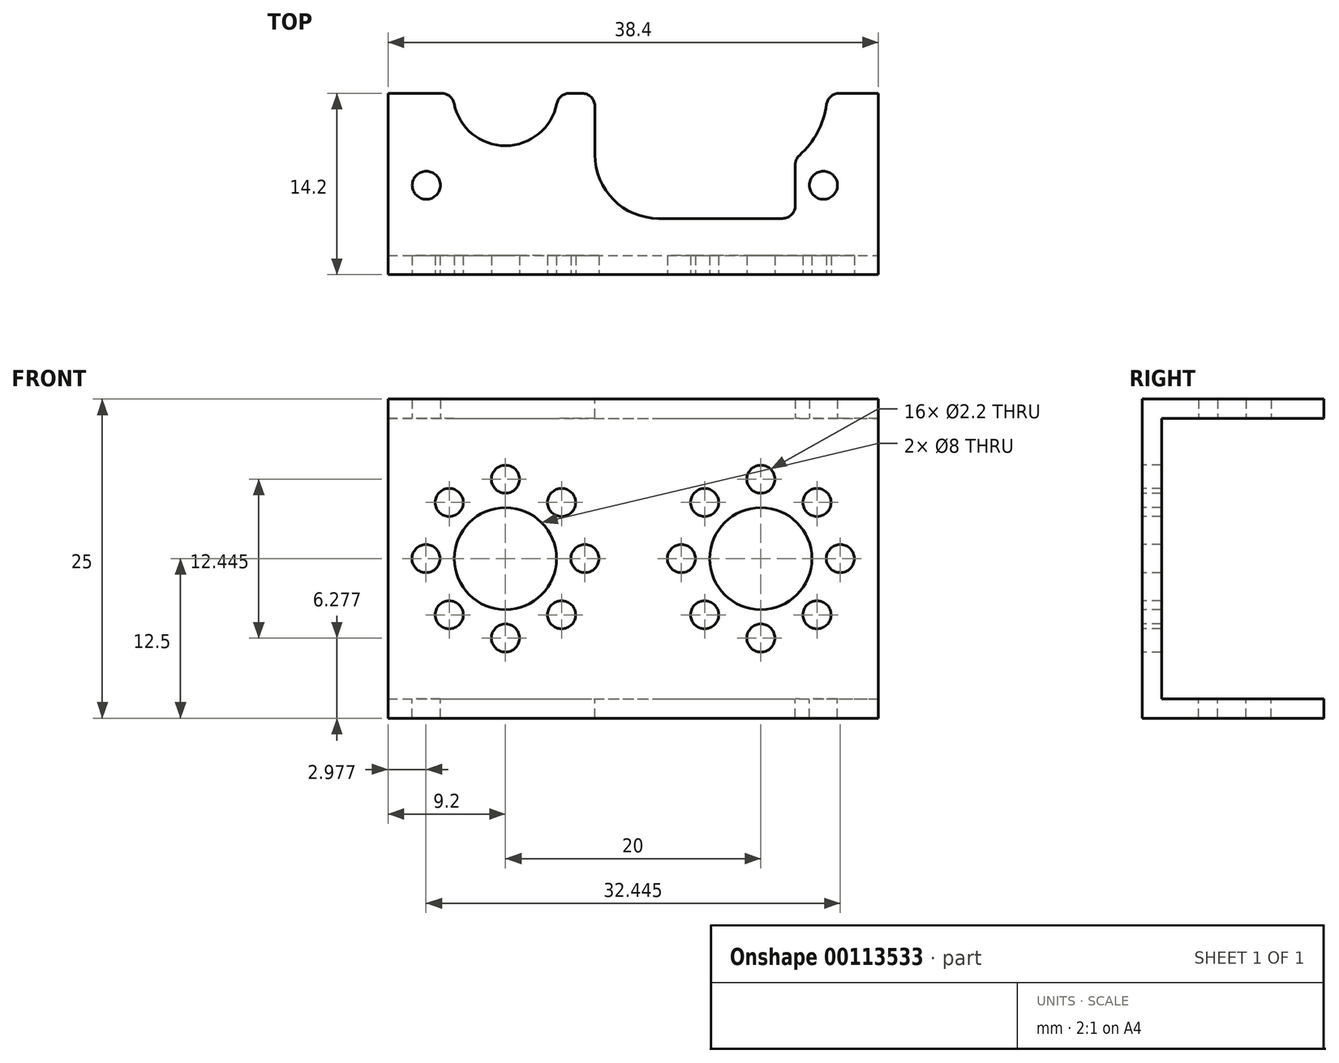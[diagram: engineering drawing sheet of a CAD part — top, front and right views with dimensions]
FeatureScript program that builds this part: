
annotation { "Feature Type Name" : "Feature", "Feature Type Description" : "" }
export const myFeature = defineFeature(function(context is Context, id is Id, definition is map)
    precondition{}
    {
        {
            var Q0;
            Q0=qCreatedBy(makeId("Top.planeOp"),FACE);
            var sketch = newSketch(context, id + "F0", { "sketchPlane" : qUnion([Q0])});
            skLineSegment(sketch, "E0.bottom", {"start": v(19.2, -14.2) * mm, "end": v(-19.2, -14.2) * mm});
            skLineSegment(sketch, "E0.top", {"start": v(19.2, 14.2) * mm, "end": v(-19.2, 14.2) * mm});
            skLineSegment(sketch, "E0.left", {"start": v(19.2, -14.2) * mm, "end": v(19.2, 14.2) * mm});
            skLineSegment(sketch, "E0.right", {"start": v(-19.2, -14.2) * mm, "end": v(-19.2, 14.2) * mm});
            skPoint(sketch, "E0.middle", {"position": v(0, 0) * mm});
            skCircle(sketch, "E1", {"center": v(-10, 0) * mm, "radius": 4.1 * mm});
            skCircle(sketch, "E2", {"center": v(-16.2, 7.2) * mm, "radius": 1.1 * mm});
            skCircle(sketch, "E3", {"center": v(14.9, 7.2) * mm, "radius": 1.1 * mm});
            skLineSegment(sketch, "E4.bottom", {"start": v(2, 9.8) * mm, "end": v(11.7, 9.8) * mm});
            skLineSegment(sketch, "E4.top", {"start": v(2, -9.8) * mm, "end": v(11.7, -9.8) * mm});
            skLineSegment(sketch, "E4.left", {"start": v(-3, 4.8) * mm, "end": v(-3, -4.8) * mm});
            skLineSegment(sketch, "E4.right", {"start": v(12.7, 8.8) * mm, "end": v(12.7, 5.6) * mm});
            skPoint(sketch, "E4.middle", {"position": v(4.85, 0) * mm});
            skPoint(sketch, "E5.visualSharp", {"position": v(-3, 9.8) * mm});
            skArc(sketch, "E5.filletArc", {"start": v(2, 9.8) * mm, "mid": v(-1.54, 8.34) * mm, "end": v(-3, 4.8) * mm});
            skPoint(sketch, "E6.visualSharp", {"position": v(-3, -9.8) * mm});
            skArc(sketch, "E6.filletArc", {"start": v(-3, -4.8) * mm, "mid": v(-1.54, -8.34) * mm, "end": v(2, -9.8) * mm});
            skPoint(sketch, "E7.visualSharp", {"position": v(12.7, 9.8) * mm});
            skArc(sketch, "E7.filletArc", {"start": v(12.7, 8.8) * mm, "mid": v(12.4, 9.5) * mm, "end": v(11.7, 9.8) * mm});
            skPoint(sketch, "E8.visualSharp", {"position": v(12.7, -9.8) * mm});
            skArc(sketch, "E8.filletArc", {"start": v(11.7, -9.8) * mm, "mid": v(12.4, -9.5) * mm, "end": v(12.7, -8.8) * mm});
            skCircle(sketch, "E9.MirrorC", {"center": v(-16.2, -7.2) * mm, "radius": 1.1 * mm});
            skCircle(sketch, "E10.MirrorC", {"center": v(14.9, -7.2) * mm, "radius": 1.1 * mm});
            skArc(sketch, "E11", {"start": v(13.03, -4.84) * mm, "mid": v(15.2, 0) * mm, "end": v(13.03, 4.84) * mm});
            skLineSegment(sketch, "E12.trimOffspring", {"start": v(12.7, -5.6) * mm, "end": v(12.7, -8.8) * mm});
            skPoint(sketch, "E13.visualSharp", {"position": v(12.7, 5.12) * mm});
            skArc(sketch, "E13.filletArc", {"start": v(12.7, 5.6) * mm, "mid": v(12.79, 5.18) * mm, "end": v(13.03, 4.84) * mm});
            skPoint(sketch, "E14.visualSharp", {"position": v(12.7, -5.12) * mm});
            skArc(sketch, "E14.filletArc", {"start": v(13.03, -4.84) * mm, "mid": v(12.79, -5.18) * mm, "end": v(12.7, -5.6) * mm});
            skSolve(sketch);
        }
        {
            var Q0;
            Q0=qSketchRegion(id+"F0",true);
            extrude(context, id + "F1", {"entities" : qUnion([Q0]), "depth" : 1.5 * mm});
        }
        {
            var Q0;
            Q0=makeQuery(id+"F1.opExtrude","CAP_FACE",FACE,{"disambiguationData":[OSD([sQuery(id+"F0.wireOp",EDGE,"E0.bottom"),sQuery(id+"F0.wireOp",EDGE,"E0.top"),sQuery(id+"F0.wireOp",EDGE,"E0.left"),sQuery(id+"F0.wireOp",EDGE,"E0.right"),sQuery(id+"F0.wireOp",EDGE,"E1"),sQuery(id+"F0.wireOp",EDGE,"E2"),sQuery(id+"F0.wireOp",EDGE,"E3"),sQuery(id+"F0.wireOp",EDGE,"E4.bottom"),sQuery(id+"F0.wireOp",EDGE,"E4.top"),sQuery(id+"F0.wireOp",EDGE,"E4.left"),sQuery(id+"F0.wireOp",EDGE,"E4.right"),sQuery(id+"F0.wireOp",EDGE,"E5.filletArc"),sQuery(id+"F0.wireOp",EDGE,"E6.filletArc"),sQuery(id+"F0.wireOp",EDGE,"E7.filletArc"),sQuery(id+"F0.wireOp",EDGE,"E8.filletArc"),sQuery(id+"F0.wireOp",EDGE,"E9.MirrorC"),sQuery(id+"F0.wireOp",EDGE,"E10.MirrorC"),sQuery(id+"F0.wireOp",EDGE,"E11"),sQuery(id+"F0.wireOp",EDGE,"E12.trimOffspring"),sQuery(id+"F0.wireOp",EDGE,"E13.filletArc"),sQuery(id+"F0.wireOp",EDGE,"E14.filletArc")])],"isStart":true});
            var sketch = newSketch(context, id + "F2", { "sketchPlane" : qUnion([Q0])});
            skLineSegment(sketch, "E15.bottom", {"start": v(-19.2, 14.2) * mm, "end": v(19.2, 14.2) * mm});
            skLineSegment(sketch, "E15.top", {"start": v(-19.2, 12.7) * mm, "end": v(19.2, 12.7) * mm});
            skLineSegment(sketch, "E15.left", {"start": v(-19.2, 14.2) * mm, "end": v(-19.2, 12.7) * mm});
            skLineSegment(sketch, "E15.right", {"start": v(19.2, 14.2) * mm, "end": v(19.2, 12.7) * mm});
            skSolve(sketch);
        }
        {
            var Q0;
            Q0=qSketchRegion(id+"F2",true);
            extrude(context, id + "F3", {"entities" : qUnion([Q0]), "operationType" : NewBodyOperationType.ADD, "depth" : (29.3 - 3.8 - 3.5) * mm});
        }
        {
            var Q0;
            Q0=qCreatedBy(makeId("Top.planeOp"),FACE);
            cPlane(context, id + "F4", {"entities" : qUnion([Q0]), "cplaneType" : CPlaneType.OFFSET, "offset" : 11 * mm, "oppositeDirection" : true, "width" : 150 * mm, "height" : 150 * mm});
        }
        {
            var Q0;
            Q0=makeQuery(id+"F1.opExtrude","SWEPT_BODY",BODY,{"disambiguationData":[OSD([sQuery(id+"F0.wireOp",EDGE,"E0.bottom"),sQuery(id+"F0.wireOp",EDGE,"E0.top"),sQuery(id+"F0.wireOp",EDGE,"E0.left"),sQuery(id+"F0.wireOp",EDGE,"E0.right"),sQuery(id+"F0.wireOp",EDGE,"E1"),sQuery(id+"F0.wireOp",EDGE,"E2"),sQuery(id+"F0.wireOp",EDGE,"E3"),sQuery(id+"F0.wireOp",EDGE,"E4.bottom"),sQuery(id+"F0.wireOp",EDGE,"E4.top"),sQuery(id+"F0.wireOp",EDGE,"E4.left"),sQuery(id+"F0.wireOp",EDGE,"E4.right"),sQuery(id+"F0.wireOp",EDGE,"E5.filletArc"),sQuery(id+"F0.wireOp",EDGE,"E6.filletArc"),sQuery(id+"F0.wireOp",EDGE,"E7.filletArc"),sQuery(id+"F0.wireOp",EDGE,"E8.filletArc"),sQuery(id+"F0.wireOp",EDGE,"E9.MirrorC"),sQuery(id+"F0.wireOp",EDGE,"E10.MirrorC"),sQuery(id+"F0.wireOp",EDGE,"E11"),sQuery(id+"F0.wireOp",EDGE,"E12.trimOffspring"),sQuery(id+"F0.wireOp",EDGE,"E13.filletArc"),sQuery(id+"F0.wireOp",EDGE,"E14.filletArc")])]});
            var Q1;
            Q1=qCreatedBy(id+"F4.planeOp",FACE);
            mirror(context, id + "F5", {"operationType" : NewBodyOperationType.ADD, "entities" : qUnion([Q0]), "mirrorPlane" : qUnion([Q1])});
        }
        {
            var Q0;
            Q0=makeQuery(id+"F5.opPattern","COPY",FACE,{"derivedFrom":makeQuery(id+"F1.opExtrude","CAP_FACE",FACE,{"disambiguationData":[OSD([sQuery(id+"F0.wireOp",EDGE,"E0.bottom"),sQuery(id+"F0.wireOp",EDGE,"E0.top"),sQuery(id+"F0.wireOp",EDGE,"E0.left"),sQuery(id+"F0.wireOp",EDGE,"E0.right"),sQuery(id+"F0.wireOp",EDGE,"E1"),sQuery(id+"F0.wireOp",EDGE,"E2"),sQuery(id+"F0.wireOp",EDGE,"E3"),sQuery(id+"F0.wireOp",EDGE,"E4.bottom"),sQuery(id+"F0.wireOp",EDGE,"E4.top"),sQuery(id+"F0.wireOp",EDGE,"E4.left"),sQuery(id+"F0.wireOp",EDGE,"E4.right"),sQuery(id+"F0.wireOp",EDGE,"E5.filletArc"),sQuery(id+"F0.wireOp",EDGE,"E6.filletArc"),sQuery(id+"F0.wireOp",EDGE,"E7.filletArc"),sQuery(id+"F0.wireOp",EDGE,"E8.filletArc"),sQuery(id+"F0.wireOp",EDGE,"E9.MirrorC"),sQuery(id+"F0.wireOp",EDGE,"E10.MirrorC"),sQuery(id+"F0.wireOp",EDGE,"E11"),sQuery(id+"F0.wireOp",EDGE,"E12.trimOffspring"),sQuery(id+"F0.wireOp",EDGE,"E13.filletArc"),sQuery(id+"F0.wireOp",EDGE,"E14.filletArc")])],"isStart":false}),"instanceName":"1"});
            var sketch = newSketch(context, id + "F6", { "sketchPlane" : qUnion([Q0])});
            skLineSegment(sketch, "E16.bottom", {"start": v(-19.2, -14.2) * mm, "end": v(19.2, -14.2) * mm});
            skLineSegment(sketch, "E16.top", {"start": v(-19.2, 0) * mm, "end": v(19.2, 0) * mm});
            skLineSegment(sketch, "E16.left", {"start": v(-19.2, -14.2) * mm, "end": v(-19.2, 0) * mm});
            skLineSegment(sketch, "E16.right", {"start": v(19.2, -14.2) * mm, "end": v(19.2, 0) * mm});
            skSolve(sketch);
        }
        {
            var Q0;
            Q0=qSketchRegion(id+"F6",true);
            extrude(context, id + "F7", {"entities" : qUnion([Q0]), "operationType" : NewBodyOperationType.REMOVE, "endBound" : BoundingType.THROUGH_ALL, "oppositeDirection" : true, "depth" : 25 * mm});
        }
        {
            var Q0;
            {var subQ0=makeQuery(id+"F3.boolean.opBoolean","MERGE",FACE,{"derivedFrom":[makeQuery(id+"F1.opExtrude","SWEPT_FACE",FACE,{"disambiguationData":[OSD([sQuery(id+"F0.wireOp",EDGE,"E0.bottom")])]}),makeQuery(id+"F3.opExtrude","SWEPT_FACE",FACE,{"disambiguationData":[OSD([sQuery(id+"F2.wireOp",EDGE,"E15.bottom")])]})]});Q0=makeQuery(id+"F5.boolean.opBoolean","MERGE",FACE,{"derivedFrom":[subQ0,makeQuery(id+"F5.opPattern","COPY",FACE,{"derivedFrom":subQ0,"instanceName":"1"})]});}
            var sketch = newSketch(context, id + "F8", { "sketchPlane" : qUnion([Q0])});
            skLineSegment(sketch, "E17", {"start": v(-19.2, -11) * mm, "end": v(19.2, -11) * mm, "construction": true});
            skLineSegment(sketch, "E18.bottom", {"start": v(-9, -2) * mm, "end": v(9, -2) * mm, "construction": true});
            skLineSegment(sketch, "E18.top", {"start": v(-9, -20) * mm, "end": v(9, -20) * mm, "construction": true});
            skLineSegment(sketch, "E18.left", {"start": v(-9, -2) * mm, "end": v(-9, -20) * mm, "construction": true});
            skLineSegment(sketch, "E18.right", {"start": v(9, -2) * mm, "end": v(9, -20) * mm, "construction": true});
            skCircle(sketch, "E19", {"center": v(9, -2) * mm, "radius": 1.1 * mm, "construction": true});
            skCircle(sketch, "E20.MirrorC", {"center": v(-9, -2) * mm, "radius": 1.1 * mm, "construction": true});
            skCircle(sketch, "E21.MirrorC", {"center": v(-9, -20) * mm, "radius": 1.1 * mm, "construction": true});
            skCircle(sketch, "E22.MirrorC", {"center": v(9, -20) * mm, "radius": 1.1 * mm, "construction": true});
            skPoint(sketch, "E23", {"position": v(0, -2) * mm});
            skPoint(sketch, "E24", {"position": v(0, -11) * mm});
            skPoint(sketch, "E25", {"position": v(-9, -11) * mm});
            skLineSegment(sketch, "E26.bottom", {"start": v(-5.6, -6.6) * mm, "end": v(-14.4, -6.6) * mm, "construction": true});
            skLineSegment(sketch, "E26.top", {"start": v(-5.6, -15.4) * mm, "end": v(-14.4, -15.4) * mm, "construction": true});
            skLineSegment(sketch, "E26.left", {"start": v(-5.6, -6.6) * mm, "end": v(-5.6, -15.4) * mm, "construction": true});
            skLineSegment(sketch, "E26.right", {"start": v(-14.4, -6.6) * mm, "end": v(-14.4, -15.4) * mm, "construction": true});
            skPoint(sketch, "E26.middle", {"position": v(-10, -11) * mm});
            skCircle(sketch, "E27", {"center": v(-10, -11) * mm, "radius": 4 * mm});
            skCircle(sketch, "E28", {"center": v(-5.6, -6.6) * mm, "radius": 1.1 * mm});
            skCircle(sketch, "E29.1.0", {"center": v(-10, -4.78) * mm, "radius": 1.1 * mm});
            skCircle(sketch, "E29.2.0", {"center": v(-14.4, -6.6) * mm, "radius": 1.1 * mm});
            skCircle(sketch, "E29.3.0", {"center": v(-16.22, -11) * mm, "radius": 1.1 * mm});
            skCircle(sketch, "E29.4.0", {"center": v(-14.4, -15.4) * mm, "radius": 1.1 * mm});
            skCircle(sketch, "E29.5.0", {"center": v(-10, -17.22) * mm, "radius": 1.1 * mm});
            skCircle(sketch, "E29.6.0", {"center": v(-5.6, -15.4) * mm, "radius": 1.1 * mm});
            skCircle(sketch, "E29.7.0", {"center": v(-3.78, -11) * mm, "radius": 1.1 * mm});
            skPoint(sketch, "E30.MirrorP", {"position": v(10, -11) * mm});
            skCircle(sketch, "E31.MirrorC", {"center": v(10, -4.78) * mm, "radius": 1.1 * mm});
            skCircle(sketch, "E32.MirrorC", {"center": v(14.4, -15.4) * mm, "radius": 1.1 * mm});
            skLineSegment(sketch, "E33.MirrorCS", {"start": v(5.6, -6.6) * mm, "end": v(5.6, -15.4) * mm, "construction": true});
            skCircle(sketch, "E34.MirrorC", {"center": v(3.78, -11) * mm, "radius": 1.1 * mm});
            skPoint(sketch, "E35.MirrorP", {"position": v(9, -11) * mm});
            skCircle(sketch, "E36.MirrorC", {"center": v(16.22, -11) * mm, "radius": 1.1 * mm});
            skCircle(sketch, "E37.MirrorC", {"center": v(5.6, -15.4) * mm, "radius": 1.1 * mm});
            skCircle(sketch, "E38.MirrorC", {"center": v(14.4, -6.6) * mm, "radius": 1.1 * mm});
            skCircle(sketch, "E39.MirrorC", {"center": v(10, -17.22) * mm, "radius": 1.1 * mm});
            skLineSegment(sketch, "E40.MirrorCS", {"start": v(14.4, -6.6) * mm, "end": v(14.4, -15.4) * mm, "construction": true});
            skCircle(sketch, "E41.MirrorC", {"center": v(10, -11) * mm, "radius": 4 * mm});
            skLineSegment(sketch, "E42.MirrorCS", {"start": v(5.6, -6.6) * mm, "end": v(14.4, -6.6) * mm, "construction": true});
            skLineSegment(sketch, "E43.MirrorCS", {"start": v(5.6, -15.4) * mm, "end": v(14.4, -15.4) * mm, "construction": true});
            skCircle(sketch, "E44.MirrorC", {"center": v(5.6, -6.6) * mm, "radius": 1.1 * mm});
            skSolve(sketch);
        }
        {
            var Q0;
            Q0=qSketchRegion(id+"F8",true);
            extrude(context, id + "F9", {"entities" : qUnion([Q0]), "operationType" : NewBodyOperationType.REMOVE, "endBound" : BoundingType.UP_TO_NEXT, "oppositeDirection" : true, "depth" : 25 * mm});
        }
        {
            var Q0;
            Q0=makeQuery(id+"F7.boolean.opBoolean","COPY",EDGE,{"disambiguationData":[OD(0.0)],"derivedFrom":makeQuery(id+"F7.opExtrude","SWEPT_EDGE",EDGE,{"disambiguationData":[OSD([sQuery(id+"F0.wireOp",EDGE,"E0.right"),sQuery(id+"F6.wireOp",EDGE,"E16.top"),sQuery(id+"F6.wireOp",EDGE,"E16.left")])]})});
            var Q1;
            Q1=makeQuery(id+"F7.boolean.opBoolean","COPY",EDGE,{"disambiguationData":[OD(1.0)],"derivedFrom":makeQuery(id+"F7.opExtrude","SWEPT_EDGE",EDGE,{"disambiguationData":[OSD([sQuery(id+"F0.wireOp",EDGE,"E0.right"),sQuery(id+"F6.wireOp",EDGE,"E16.top"),sQuery(id+"F6.wireOp",EDGE,"E16.left")])]})});
            var Q2;
            Q2=makeQuery(id+"F7.boolean.opBoolean","INTERSECT",EDGE,{"disambiguationData":[OD(1.0)],"derivedFrom":[makeQuery(id+"F1.opExtrude","SWEPT_FACE",FACE,{"disambiguationData":[OSD([sQuery(id+"F0.wireOp",EDGE,"E1")])]}),makeQuery(id+"F7.opExtrude","SWEPT_FACE",FACE,{"disambiguationData":[OSD([sQuery(id+"F6.wireOp",EDGE,"E16.top")])]})]});
            var Q3;
            Q3=makeQuery(id+"F7.boolean.opBoolean","INTERSECT",EDGE,{"disambiguationData":[OD(1.0)],"derivedFrom":[makeQuery(id+"F5.opPattern","COPY",FACE,{"derivedFrom":makeQuery(id+"F1.opExtrude","SWEPT_FACE",FACE,{"disambiguationData":[OSD([sQuery(id+"F0.wireOp",EDGE,"E1")])]}),"instanceName":"1"}),makeQuery(id+"F7.opExtrude","SWEPT_FACE",FACE,{"disambiguationData":[OSD([sQuery(id+"F6.wireOp",EDGE,"E16.top")])]})]});
            var Q4;
            Q4=makeQuery(id+"F7.boolean.opBoolean","INTERSECT",EDGE,{"disambiguationData":[OD(0.0)],"derivedFrom":[makeQuery(id+"F5.opPattern","COPY",FACE,{"derivedFrom":makeQuery(id+"F1.opExtrude","SWEPT_FACE",FACE,{"disambiguationData":[OSD([sQuery(id+"F0.wireOp",EDGE,"E1")])]}),"instanceName":"1"}),makeQuery(id+"F7.opExtrude","SWEPT_FACE",FACE,{"disambiguationData":[OSD([sQuery(id+"F6.wireOp",EDGE,"E16.top")])]})]});
            var Q5;
            Q5=makeQuery(id+"F7.boolean.opBoolean","INTERSECT",EDGE,{"derivedFrom":[makeQuery(id+"F5.opPattern","COPY",FACE,{"derivedFrom":makeQuery(id+"F1.opExtrude","SWEPT_FACE",FACE,{"disambiguationData":[OSD([sQuery(id+"F0.wireOp",EDGE,"E4.left")])]}),"instanceName":"1"}),makeQuery(id+"F7.opExtrude","SWEPT_FACE",FACE,{"disambiguationData":[OSD([sQuery(id+"F6.wireOp",EDGE,"E16.top")])]})]});
            var Q6;
            Q6=makeQuery(id+"F7.boolean.opBoolean","INTERSECT",EDGE,{"disambiguationData":[OD(0.0)],"derivedFrom":[makeQuery(id+"F1.opExtrude","SWEPT_FACE",FACE,{"disambiguationData":[OSD([sQuery(id+"F0.wireOp",EDGE,"E1")])]}),makeQuery(id+"F7.opExtrude","SWEPT_FACE",FACE,{"disambiguationData":[OSD([sQuery(id+"F6.wireOp",EDGE,"E16.top")])]})]});
            var Q7;
            Q7=makeQuery(id+"F7.boolean.opBoolean","INTERSECT",EDGE,{"derivedFrom":[makeQuery(id+"F5.opPattern","COPY",FACE,{"derivedFrom":makeQuery(id+"F1.opExtrude","SWEPT_FACE",FACE,{"disambiguationData":[OSD([sQuery(id+"F0.wireOp",EDGE,"E11")])]}),"instanceName":"1"}),makeQuery(id+"F7.opExtrude","SWEPT_FACE",FACE,{"disambiguationData":[OSD([sQuery(id+"F6.wireOp",EDGE,"E16.top")])]})]});
            var Q8;
            Q8=makeQuery(id+"F7.boolean.opBoolean","INTERSECT",EDGE,{"derivedFrom":[makeQuery(id+"F1.opExtrude","SWEPT_FACE",FACE,{"disambiguationData":[OSD([sQuery(id+"F0.wireOp",EDGE,"E11")])]}),makeQuery(id+"F7.opExtrude","SWEPT_FACE",FACE,{"disambiguationData":[OSD([sQuery(id+"F6.wireOp",EDGE,"E16.top")])]})]});
            var Q9;
            Q9=makeQuery(id+"F7.boolean.opBoolean","COPY",EDGE,{"disambiguationData":[OD(0.0)],"derivedFrom":makeQuery(id+"F7.opExtrude","SWEPT_EDGE",EDGE,{"disambiguationData":[OSD([sQuery(id+"F0.wireOp",EDGE,"E0.left"),sQuery(id+"F6.wireOp",EDGE,"E16.top"),sQuery(id+"F6.wireOp",EDGE,"E16.right")])]})});
            var Q10;
            Q10=makeQuery(id+"F7.boolean.opBoolean","INTERSECT",EDGE,{"derivedFrom":[makeQuery(id+"F1.opExtrude","SWEPT_FACE",FACE,{"disambiguationData":[OSD([sQuery(id+"F0.wireOp",EDGE,"E4.left")])]}),makeQuery(id+"F7.opExtrude","SWEPT_FACE",FACE,{"disambiguationData":[OSD([sQuery(id+"F6.wireOp",EDGE,"E16.top")])]})]});
            var Q11;
            Q11=makeQuery(id+"F7.boolean.opBoolean","COPY",EDGE,{"disambiguationData":[OD(1.0)],"derivedFrom":makeQuery(id+"F7.opExtrude","SWEPT_EDGE",EDGE,{"disambiguationData":[OSD([sQuery(id+"F0.wireOp",EDGE,"E0.left"),sQuery(id+"F6.wireOp",EDGE,"E16.top"),sQuery(id+"F6.wireOp",EDGE,"E16.right")])]})});
            fillet(context, id + "F10", {"entities" : qUnion([Q0, Q1, Q2, Q3, Q4, Q5, Q6, Q7, Q8, Q9, Q10, Q11]), "radius" : 1 * mm, "tangentPropagation" : true, "allowEdgeOverflow" : false});
        }
    });
